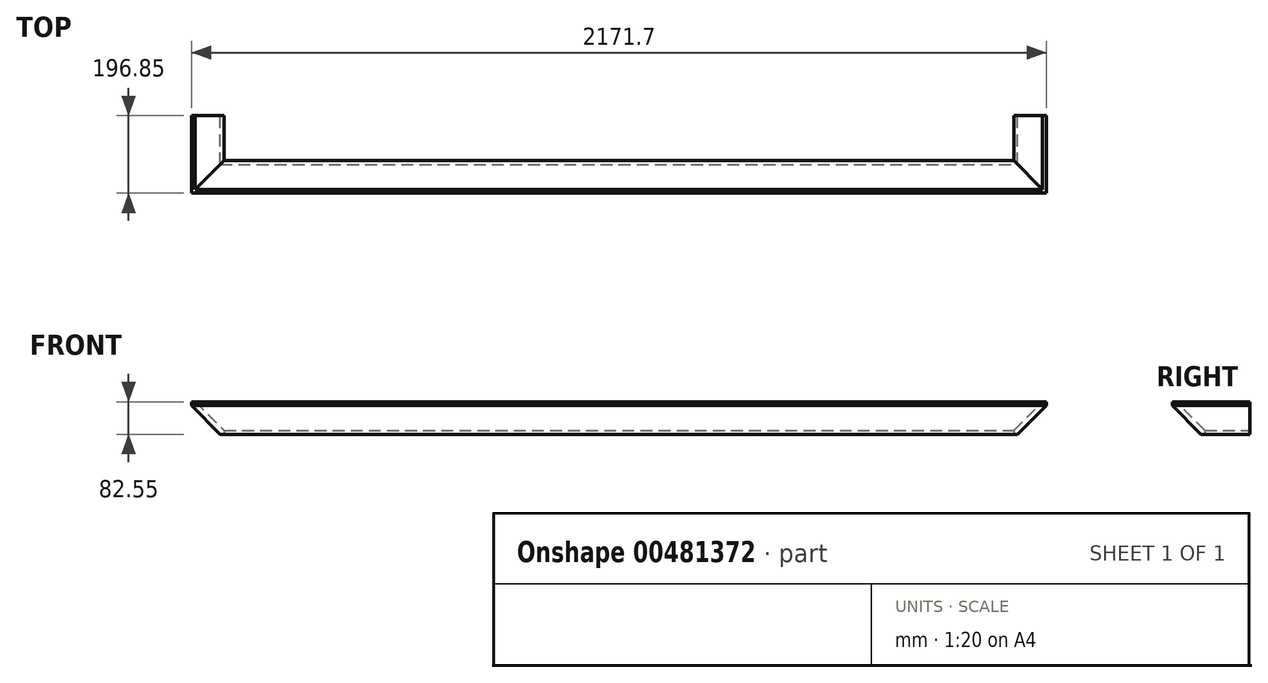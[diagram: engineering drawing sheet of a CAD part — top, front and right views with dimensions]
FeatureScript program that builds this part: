
annotation { "Feature Type Name" : "Feature", "Feature Type Description" : "" }
export const myFeature = defineFeature(function(context is Context, id is Id, definition is map)
    precondition{}
    {
        {
            var Q0;
            Q0=qCreatedBy(makeId("Top.planeOp"),FACE);
            var sketch = newSketch(context, id + "F0", { "sketchPlane" : qUnion([Q0])});
            skLineSegment(sketch, "E0.bottom", {"start": v(0, 0) * mm, "end": v(203.2, 0) * mm});
            skLineSegment(sketch, "E0.top", {"start": v(0, 101.6) * mm, "end": v(203.2, 101.6) * mm});
            skLineSegment(sketch, "E0.left", {"start": v(0, 0) * mm, "end": v(0, 101.6) * mm});
            skLineSegment(sketch, "E0.right", {"start": v(203.2, 0) * mm, "end": v(203.2, 101.6) * mm});
            skLineSegment(sketch, "E1.bottom", {"start": v(1778, 0) * mm, "end": v(1981.2, 0) * mm});
            skLineSegment(sketch, "E1.top", {"start": v(1778, 101.6) * mm, "end": v(1981.2, 101.6) * mm});
            skLineSegment(sketch, "E1.left", {"start": v(1778, 0) * mm, "end": v(1778, 101.6) * mm});
            skLineSegment(sketch, "E1.right", {"start": v(1981.2, 0) * mm, "end": v(1981.2, 101.6) * mm});
            skSolve(sketch);
        }
        {
            var Q0;
            Q0=makeQuery(id+"F0.imprint","IMPRINT",FACE,{"disambiguationData":[TD([[makeQuery(id+"F0.imprint","IMPRINT",EDGE,{"derivedFrom":sQuery(id+"F0.wireOp",EDGE,"E0.bottom")}),1.0]])]});
            var Q1;
            Q1=makeQuery(id+"F0.imprint","IMPRINT",FACE,{"disambiguationData":[TD([[makeQuery(id+"F0.imprint","IMPRINT",EDGE,{"derivedFrom":sQuery(id+"F0.wireOp",EDGE,"E1.bottom")}),1.0]])]});
            extrude(context, id + "F1", {"entities" : qUnion([Q0, Q1]), "depth" : 1485.9 * mm});
        }
        {
            var Q0;
            Q0=qCreatedBy(makeId("Right.planeOp"),FACE);
            var sketch = newSketch(context, id + "F2", { "sketchPlane" : qUnion([Q0])});
            skLineSegment(sketch, "E2.bottom", {"start": v(101.6, 1485.9) * mm, "end": v(-127, 1485.9) * mm});
            skLineSegment(sketch, "E2.top", {"start": v(101.6, 1524) * mm, "end": v(-127, 1524) * mm});
            skLineSegment(sketch, "E2.left", {"start": v(101.6, 1485.9) * mm, "end": v(101.6, 1524) * mm});
            skLineSegment(sketch, "E2.right", {"start": v(-127, 1485.9) * mm, "end": v(-127, 1524) * mm});
            skSolve(sketch);
        }
        {
            var Q0;
            Q0 = qSketchRegion(id + "F2", true);
            extrude(context, id + "F3", {"entities" : qUnion([Q0]), "depth" : 2108.2 * mm, "hasSecondDirection" : true, "secondDirectionOppositeDirection" : true, "secondDirectionDepth" : 127 * mm});
        }
        {
            var Q0;
            Q0=qCreatedBy(makeId("Top.planeOp"),FACE);
            var sketch = newSketch(context, id + "F4", { "sketchPlane" : qUnion([Q0])});
            skLineSegment(sketch, "E3.bottom", {"start": v(-25.4, 101.6) * mm, "end": v(228.6, 101.6) * mm});
            skLineSegment(sketch, "E3.top", {"start": v(-25.4, -25.4) * mm, "end": v(228.6, -25.4) * mm});
            skLineSegment(sketch, "E3.left", {"start": v(-25.4, 101.6) * mm, "end": v(-25.4, -25.4) * mm});
            skLineSegment(sketch, "E3.right", {"start": v(228.6, 101.6) * mm, "end": v(228.6, -25.4) * mm});
            skLineSegment(sketch, "E4.bottom", {"start": v(1752.6, 101.6) * mm, "end": v(2006.6, 101.6) * mm});
            skLineSegment(sketch, "E4.top", {"start": v(1752.6, -25.4) * mm, "end": v(2006.6, -25.4) * mm});
            skLineSegment(sketch, "E4.left", {"start": v(1752.6, 101.6) * mm, "end": v(1752.6, -25.4) * mm});
            skLineSegment(sketch, "E4.right", {"start": v(2006.6, 101.6) * mm, "end": v(2006.6, -25.4) * mm});
            skSolve(sketch);
        }
        {
            var Q0;
            Q0 = qSketchRegion(id + "F4", true);
            extrude(context, id + "F5", {"entities" : qUnion([Q0]), "depth" : 152.4 * mm});
        }
        {
            var Q0;
            Q0=makeQuery(id+"F5.opExtrude","CAP_FACE",FACE,{"disambiguationData":[OSD([sQuery(id+"F4.wireOp",EDGE,"E3.bottom"),sQuery(id+"F4.wireOp",EDGE,"E3.top"),sQuery(id+"F4.wireOp",EDGE,"E3.left"),sQuery(id+"F4.wireOp",EDGE,"E3.right")])],"isStart":false});
            var sketch = newSketch(context, id + "F6", { "sketchPlane" : qUnion([Q0])});
            skLineSegment(sketch, "E5.bottom", {"start": v(-12.7, 101.6) * mm, "end": v(215.9, 101.6) * mm});
            skLineSegment(sketch, "E5.top", {"start": v(-12.7, -12.7) * mm, "end": v(215.9, -12.7) * mm});
            skLineSegment(sketch, "E5.left", {"start": v(-12.7, 101.6) * mm, "end": v(-12.7, -12.7) * mm});
            skLineSegment(sketch, "E5.right", {"start": v(215.9, 101.6) * mm, "end": v(215.9, -12.7) * mm});
            skLineSegment(sketch, "E6.bottom", {"start": v(1765.3, 101.6) * mm, "end": v(1993.9, 101.6) * mm});
            skLineSegment(sketch, "E6.top", {"start": v(1765.3, -12.7) * mm, "end": v(1993.9, -12.7) * mm});
            skLineSegment(sketch, "E6.left", {"start": v(1765.3, 101.6) * mm, "end": v(1765.3, -12.7) * mm});
            skLineSegment(sketch, "E6.right", {"start": v(1993.9, 101.6) * mm, "end": v(1993.9, -12.7) * mm});
            skSolve(sketch);
        }
        {
            var Q0;
            Q0 = qSketchRegion(id + "F6", true);
            extrude(context, id + "F7", {"entities" : qUnion([Q0]), "depth" : 50.8 * mm});
        }
        {
            var Q0;
            Q0=makeQuery(id+"F7.opExtrude","CAP_FACE",FACE,{"disambiguationData":[OSD([sQuery(id+"F6.wireOp",EDGE,"E5.bottom"),sQuery(id+"F6.wireOp",EDGE,"E5.top"),sQuery(id+"F6.wireOp",EDGE,"E5.left"),sQuery(id+"F6.wireOp",EDGE,"E5.right")])],"isStart":false});
            var sketch = newSketch(context, id + "F8", { "sketchPlane" : qUnion([Q0])});
            skLineSegment(sketch, "E7.bottom", {"start": v(-12.7, -12.7) * mm, "end": v(50.8, -12.7) * mm});
            skLineSegment(sketch, "E7.top", {"start": v(-12.7, 38.1) * mm, "end": v(50.8, 38.1) * mm});
            skLineSegment(sketch, "E7.left", {"start": v(-12.7, -12.7) * mm, "end": v(-12.7, 38.1) * mm});
            skLineSegment(sketch, "E7.right", {"start": v(50.8, -12.7) * mm, "end": v(50.8, 38.1) * mm});
            skLineSegment(sketch, "E8.bottom", {"start": v(215.9, -12.7) * mm, "end": v(152.4, -12.7) * mm});
            skLineSegment(sketch, "E8.top", {"start": v(215.9, 38.1) * mm, "end": v(152.4, 38.1) * mm});
            skLineSegment(sketch, "E8.left", {"start": v(215.9, -12.7) * mm, "end": v(215.9, 38.1) * mm});
            skLineSegment(sketch, "E8.right", {"start": v(152.4, -12.7) * mm, "end": v(152.4, 38.1) * mm});
            skLineSegment(sketch, "E9.bottom", {"start": v(-12.7, 101.6) * mm, "end": v(12.7, 101.6) * mm});
            skLineSegment(sketch, "E9.top", {"start": v(-12.7, 76.2) * mm, "end": v(12.7, 76.2) * mm});
            skLineSegment(sketch, "E9.left", {"start": v(-12.7, 101.6) * mm, "end": v(-12.7, 76.2) * mm});
            skLineSegment(sketch, "E9.right", {"start": v(12.7, 101.6) * mm, "end": v(12.7, 76.2) * mm});
            skLineSegment(sketch, "E10.bottom", {"start": v(215.9, 101.6) * mm, "end": v(190.5, 101.6) * mm});
            skLineSegment(sketch, "E10.top", {"start": v(215.9, 76.2) * mm, "end": v(190.5, 76.2) * mm});
            skLineSegment(sketch, "E10.left", {"start": v(215.9, 101.6) * mm, "end": v(215.9, 76.2) * mm});
            skLineSegment(sketch, "E10.right", {"start": v(190.5, 101.6) * mm, "end": v(190.5, 76.2) * mm});
            skLineSegment(sketch, "E11.bottom", {"start": v(1828.8, 38.1) * mm, "end": v(1765.3, 38.1) * mm});
            skLineSegment(sketch, "E11.top", {"start": v(1828.8, -12.7) * mm, "end": v(1765.3, -12.7) * mm});
            skLineSegment(sketch, "E11.left", {"start": v(1828.8, 38.1) * mm, "end": v(1828.8, -12.7) * mm});
            skLineSegment(sketch, "E11.right", {"start": v(1765.3, 38.1) * mm, "end": v(1765.3, -12.7) * mm});
            skLineSegment(sketch, "E12.bottom", {"start": v(1930.4, 38.1) * mm, "end": v(1993.9, 38.1) * mm});
            skLineSegment(sketch, "E12.top", {"start": v(1930.4, -12.7) * mm, "end": v(1993.9, -12.7) * mm});
            skLineSegment(sketch, "E12.left", {"start": v(1930.4, 38.1) * mm, "end": v(1930.4, -12.7) * mm});
            skLineSegment(sketch, "E12.right", {"start": v(1993.9, 38.1) * mm, "end": v(1993.9, -12.7) * mm});
            skLineSegment(sketch, "E13.bottom", {"start": v(1993.9, 101.6) * mm, "end": v(1968.5, 101.6) * mm});
            skLineSegment(sketch, "E13.top", {"start": v(1993.9, 76.2) * mm, "end": v(1968.5, 76.2) * mm});
            skLineSegment(sketch, "E13.left", {"start": v(1993.9, 101.6) * mm, "end": v(1993.9, 76.2) * mm});
            skLineSegment(sketch, "E13.right", {"start": v(1968.5, 101.6) * mm, "end": v(1968.5, 76.2) * mm});
            skLineSegment(sketch, "E14.bottom", {"start": v(1765.3, 101.6) * mm, "end": v(1790.7, 101.6) * mm});
            skLineSegment(sketch, "E14.top", {"start": v(1765.3, 76.2) * mm, "end": v(1790.7, 76.2) * mm});
            skLineSegment(sketch, "E14.left", {"start": v(1765.3, 101.6) * mm, "end": v(1765.3, 76.2) * mm});
            skLineSegment(sketch, "E14.right", {"start": v(1790.7, 101.6) * mm, "end": v(1790.7, 76.2) * mm});
            skSolve(sketch);
        }
        {
            var Q0;
            Q0 = qSketchRegion(id + "F8", true);
            extrude(context, id + "F9", {"entities" : qUnion([Q0]), "depth" : 1149.35 * mm});
        }
        {
            var Q0;
            Q0=makeQuery(id+"F9.opExtrude","CAP_FACE",FACE,{"disambiguationData":[OSD([sQuery(id+"F8.wireOp",EDGE,"E7.bottom"),sQuery(id+"F8.wireOp",EDGE,"E7.top"),sQuery(id+"F8.wireOp",EDGE,"E7.left"),sQuery(id+"F8.wireOp",EDGE,"E7.right")])],"isStart":false});
            var sketch = newSketch(context, id + "F10", { "sketchPlane" : qUnion([Q0])});
            skLineSegment(sketch, "E15.bottom", {"start": v(-12.7, -12.7) * mm, "end": v(215.9, -12.7) * mm});
            skLineSegment(sketch, "E15.top", {"start": v(-12.7, 101.6) * mm, "end": v(215.9, 101.6) * mm});
            skLineSegment(sketch, "E15.left", {"start": v(-12.7, -12.7) * mm, "end": v(-12.7, 101.6) * mm});
            skLineSegment(sketch, "E15.right", {"start": v(215.9, -12.7) * mm, "end": v(215.9, 101.6) * mm});
            skLineSegment(sketch, "E16.bottom", {"start": v(1765.3, -12.7) * mm, "end": v(1993.9, -12.7) * mm});
            skLineSegment(sketch, "E16.top", {"start": v(1765.3, 101.6) * mm, "end": v(1993.9, 101.6) * mm});
            skLineSegment(sketch, "E16.left", {"start": v(1765.3, -12.7) * mm, "end": v(1765.3, 101.6) * mm});
            skLineSegment(sketch, "E16.right", {"start": v(1993.9, -12.7) * mm, "end": v(1993.9, 101.6) * mm});
            skSolve(sketch);
        }
        {
            var Q0;
            Q0 = qSketchRegion(id + "F10", true);
            extrude(context, id + "F11", {"entities" : qUnion([Q0]), "depth" : 133.35 * mm});
        }
        {
            var Q0;
            Q0=makeQuery(id+"F11.opExtrude","CAP_FACE",FACE,{"disambiguationData":[OSD([sQuery(id+"F10.wireOp",EDGE,"E15.bottom"),sQuery(id+"F10.wireOp",EDGE,"E15.top"),sQuery(id+"F10.wireOp",EDGE,"E15.left"),sQuery(id+"F10.wireOp",EDGE,"E15.right")])],"isStart":false});
            var sketch = newSketch(context, id + "F12", { "sketchPlane" : qUnion([Q0])});
            skLineSegment(sketch, "E17.bottom", {"start": v(215.9, 101.6) * mm, "end": v(1765.3, 101.6) * mm});
            skLineSegment(sketch, "E17.top", {"start": v(215.9, 88.9) * mm, "end": v(1765.3, 88.9) * mm});
            skLineSegment(sketch, "E17.left", {"start": v(215.9, 101.6) * mm, "end": v(215.9, 88.9) * mm});
            skLineSegment(sketch, "E17.right", {"start": v(1765.3, 101.6) * mm, "end": v(1765.3, 88.9) * mm});
            skSolve(sketch);
        }
        {
            var Q0;
            Q0 = qSketchRegion(id + "F12", true);
            extrude(context, id + "F13", {"entities" : qUnion([Q0]), "oppositeDirection" : true, "depth" : 254 * mm});
        }
        {
            var Q0;
            Q0=makeQuery(id+"F13.opExtrude","CAP_FACE",FACE,{"disambiguationData":[OSD([sQuery(id+"F12.wireOp",EDGE,"E17.bottom"),sQuery(id+"F12.wireOp",EDGE,"E17.top"),sQuery(id+"F12.wireOp",EDGE,"E17.left"),sQuery(id+"F12.wireOp",EDGE,"E17.right")])],"isStart":true});
            var sketch = newSketch(context, id + "F14", { "sketchPlane" : qUnion([Q0])});
            skLineSegment(sketch, "E18.bottom", {"start": v(215.9, 88.9) * mm, "end": v(266.7, 88.9) * mm});
            skLineSegment(sketch, "E18.top", {"start": v(215.9, 76.2) * mm, "end": v(266.7, 76.2) * mm});
            skLineSegment(sketch, "E18.left", {"start": v(215.9, 88.9) * mm, "end": v(215.9, 76.2) * mm});
            skLineSegment(sketch, "E18.right", {"start": v(266.7, 88.9) * mm, "end": v(266.7, 76.2) * mm});
            skLineSegment(sketch, "E19.bottom", {"start": v(1714.5, 76.2) * mm, "end": v(1765.3, 76.2) * mm});
            skLineSegment(sketch, "E19.top", {"start": v(1714.5, 88.9) * mm, "end": v(1765.3, 88.9) * mm});
            skLineSegment(sketch, "E19.left", {"start": v(1714.5, 76.2) * mm, "end": v(1714.5, 88.9) * mm});
            skLineSegment(sketch, "E19.right", {"start": v(1765.3, 76.2) * mm, "end": v(1765.3, 88.9) * mm});
            skSolve(sketch);
        }
        {
            var Q0;
            Q0 = qSketchRegion(id + "F14", true);
            var Q1;
            Q1=makeQuery(id+"F13.opExtrude","CAP_FACE",FACE,{"disambiguationData":[OSD([sQuery(id+"F12.wireOp",EDGE,"E17.bottom"),sQuery(id+"F12.wireOp",EDGE,"E17.top"),sQuery(id+"F12.wireOp",EDGE,"E17.left"),sQuery(id+"F12.wireOp",EDGE,"E17.right")])],"isStart":false});
            extrude(context, id + "F15", {"entities" : qUnion([Q0]), "endBound" : BoundingType.UP_TO_SURFACE, "oppositeDirection" : true, "endBoundEntityFace" : qUnion([Q1]), "depth" : 254 * mm});
        }
        {
            var Q0;
            Q0=makeQuery(id+"F13.opExtrude","CAP_FACE",FACE,{"disambiguationData":[OSD([sQuery(id+"F12.wireOp",EDGE,"E17.bottom"),sQuery(id+"F12.wireOp",EDGE,"E17.top"),sQuery(id+"F12.wireOp",EDGE,"E17.left"),sQuery(id+"F12.wireOp",EDGE,"E17.right")])],"isStart":true});
            var sketch = newSketch(context, id + "F16", { "sketchPlane" : qUnion([Q0])});
            skLineSegment(sketch, "E20.bottom", {"start": v(266.7, 88.9) * mm, "end": v(1714.5, 88.9) * mm});
            skLineSegment(sketch, "E20.top", {"start": v(266.7, 76.2) * mm, "end": v(1714.5, 76.2) * mm});
            skLineSegment(sketch, "E20.left", {"start": v(266.7, 88.9) * mm, "end": v(266.7, 76.2) * mm});
            skLineSegment(sketch, "E20.right", {"start": v(1714.5, 88.9) * mm, "end": v(1714.5, 76.2) * mm});
            skSolve(sketch);
        }
        {
            var Q0;
            Q0 = qSketchRegion(id + "F16", true);
            extrude(context, id + "F17", {"entities" : qUnion([Q0]), "oppositeDirection" : true, "depth" : 146.05 * mm});
        }
        {
            var Q0;
            Q0=makeQuery(id+"F13.opExtrude","CAP_FACE",FACE,{"disambiguationData":[OSD([sQuery(id+"F12.wireOp",EDGE,"E17.bottom"),sQuery(id+"F12.wireOp",EDGE,"E17.top"),sQuery(id+"F12.wireOp",EDGE,"E17.left"),sQuery(id+"F12.wireOp",EDGE,"E17.right")])],"isStart":false});
            var sketch = newSketch(context, id + "F18", { "sketchPlane" : qUnion([Q0])});
            skLineSegment(sketch, "E21.bottom", {"start": v(266.7, -88.9) * mm, "end": v(1714.5, -88.9) * mm});
            skLineSegment(sketch, "E21.top", {"start": v(266.7, -76.2) * mm, "end": v(1714.5, -76.2) * mm});
            skLineSegment(sketch, "E21.left", {"start": v(266.7, -88.9) * mm, "end": v(266.7, -76.2) * mm});
            skLineSegment(sketch, "E21.right", {"start": v(1714.5, -88.9) * mm, "end": v(1714.5, -76.2) * mm});
            skSolve(sketch);
        }
        {
            var Q0;
            Q0 = qSketchRegion(id + "F18", true);
            extrude(context, id + "F19", {"entities" : qUnion([Q0]), "oppositeDirection" : true, "depth" : 50.8 * mm});
        }
        {
            var Q0;
            Q0=makeQuery(id+"F11.opExtrude","SWEPT_FACE",FACE,{"disambiguationData":[OSD([sQuery(id+"F10.wireOp",EDGE,"E15.left")])]});
            var sketch = newSketch(context, id + "F20", { "sketchPlane" : qUnion([Q0])});
            skLineSegment(sketch, "E22", {"start": v(12.7, 1412.88) * mm, "end": v(85.73, 1485.9) * mm});
            skLineSegment(sketch, "E23", {"start": v(85.73, 1485.9) * mm, "end": v(95.25, 1485.9) * mm});
            skLineSegment(sketch, "E24", {"start": v(95.25, 1485.9) * mm, "end": v(95.25, 1476.38) * mm});
            skLineSegment(sketch, "E25", {"start": v(12.7, 1412.88) * mm, "end": v(12.7, 1403.35) * mm});
            skLineSegment(sketch, "E26", {"start": v(12.7, 1403.35) * mm, "end": v(22.23, 1403.35) * mm});
            skLineSegment(sketch, "E27", {"start": v(22.22, 1403.35) * mm, "end": v(95.25, 1476.38) * mm});
            skSolve(sketch);
        }
        {
            var Q0;
            Q0=makeQuery(id+"F1.opExtrude","SWEPT_FACE",FACE,{"disambiguationData":[OSD([sQuery(id+"F0.wireOp",EDGE,"E0.top")])]});
            var sketch = newSketch(context, id + "F21", { "sketchPlane" : qUnion([Q0])});
            skLineSegment(sketch, "E28", {"start": v(12.7, 1412.88) * mm, "end": v(85.73, 1485.9) * mm});
            skLineSegment(sketch, "E29", {"start": v(85.72, 1485.9) * mm, "end": v(95.25, 1485.9) * mm});
            skLineSegment(sketch, "E30", {"start": v(95.25, 1485.9) * mm, "end": v(95.25, 1476.38) * mm});
            skLineSegment(sketch, "E31", {"start": v(12.7, 1412.88) * mm, "end": v(12.7, 1403.35) * mm});
            skLineSegment(sketch, "E32", {"start": v(12.7, 1403.35) * mm, "end": v(22.22, 1403.35) * mm});
            skLineSegment(sketch, "E33", {"start": v(22.22, 1403.35) * mm, "end": v(95.25, 1476.38) * mm});
            skLineSegment(sketch, "E34", {"start": v(-2076.45, 1476.38) * mm, "end": v(-2076.45, 1485.9) * mm});
            skLineSegment(sketch, "E35", {"start": v(-2076.45, 1485.9) * mm, "end": v(-2066.93, 1485.9) * mm});
            skLineSegment(sketch, "E36", {"start": v(-2066.93, 1485.9) * mm, "end": v(-1993.9, 1412.88) * mm});
            skLineSegment(sketch, "E37", {"start": v(-1993.9, 1412.88) * mm, "end": v(-1993.9, 1403.35) * mm});
            skLineSegment(sketch, "E38", {"start": v(-1993.9, 1403.35) * mm, "end": v(-2003.42, 1403.35) * mm});
            skLineSegment(sketch, "E39", {"start": v(-2003.42, 1403.35) * mm, "end": v(-2076.45, 1476.38) * mm});
            skSolve(sketch);
        }
        {
            var Q0;
            Q0=makeQuery(id+"F21.imprint","IMPRINT",FACE,{"disambiguationData":[TD([[makeQuery(id+"F21.imprint","IMPRINT",EDGE,{"derivedFrom":sQuery(id+"F21.wireOp",EDGE,"E28")}),-1.0]])]});
            var Q1;
            Q1=makeQuery(id+"F21.imprint","IMPRINT",FACE,{"disambiguationData":[TD([[makeQuery(id+"F21.imprint","IMPRINT",EDGE,{"derivedFrom":sQuery(id+"F21.wireOp",EDGE,"E34")}),-1.0]])]});
            extrude(context, id + "F22", {"entities" : qUnion([Q0, Q1]), "oppositeDirection" : true, "depth" : 254 * mm});
        }
        {
            var Q0;
            Q0=makeQuery(id+"F20.imprint","IMPRINT",FACE,{"disambiguationData":[TD([[makeQuery(id+"F20.imprint","IMPRINT",EDGE,{"derivedFrom":sQuery(id+"F20.wireOp",EDGE,"E22")}),-1.0]])]});
            extrude(context, id + "F23", {"entities" : qUnion([Q0]), "operationType" : NewBodyOperationType.INTERSECT, "depth" : 101.6 * mm, "hasSecondDirection" : true, "secondDirectionOppositeDirection" : true, "secondDirectionDepth" : 2540 * mm});
        }
        {
            var Q0;
            Q0 = qSketchRegion(id + "F21", true);
            extrude(context, id + "F24", {"entities" : qUnion([Q0]), "endBound" : BoundingType.UP_TO_NEXT, "oppositeDirection" : true, "depth" : 25.4 * mm});
        }
        {
            var Q0;
            Q0 = qSketchRegion(id + "F20", true);
            extrude(context, id + "F25", {"entities" : qUnion([Q0]), "operationType" : NewBodyOperationType.ADD, "endBound" : BoundingType.UP_TO_NEXT, "depth" : 25.4 * mm, "hasSecondDirection" : true, "secondDirectionBound" : BoundingType.UP_TO_NEXT, "secondDirectionOppositeDirection" : true, "secondDirectionDepth" : 25.4 * mm});
        }
    });
